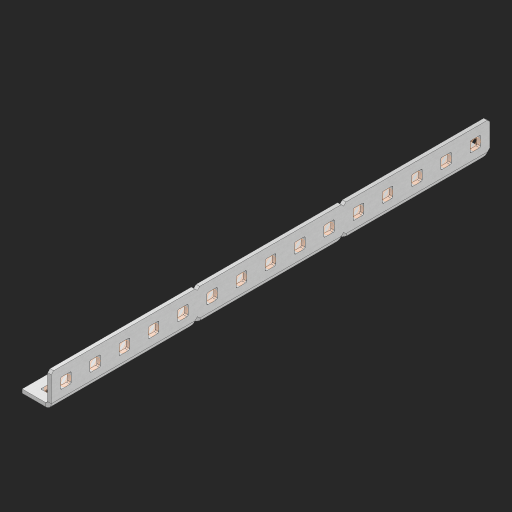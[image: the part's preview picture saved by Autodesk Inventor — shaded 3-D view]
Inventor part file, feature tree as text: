
AUTODESK INVENTOR PART (.ipt)
format: ipt  version: 2023 (Build 270158000, 158)  size: 598,528 bytes
history: native  units: in
note: dims shown in document units (in); Inventor stores cm internally (conversion verified against a paired STEP export)
features: other x35, extrude x29, sheet_metal_op x10, sketch x8, mirror x1, pattern_linear x1, chamfer x1
ambient origin geometry x8: Origin, YZ Plane, XZ Plane, XY Plane, X Axis, Y Axis, Z Axis, Center Point
bodies: Solid1 (feature_tree), Body (feature_tree)
feature tree (85):
  other  "Flange Pattern Plane"
  sheet_metal_op  "Flange Pattern"
  sheet_metal_op  "Body Pattern"
  other  "Arc Length"
  mirror  "Notch Mirror"
  pattern_linear  "Notch Pattern"  Spacing1=0.25in  [1 undecoded]
  chamfer  "End Chamfer"
  extrude  "Half Cut"  Depth=0.0625in
  sketch  "Sketch1"  dims[d0=1.5in]
  other  "Plate1"
  sketch  "Sketch2"  dims[d1=7.5in]
  other  "Plate2"
  sheet_metal_op  "Bend1"
  sheet_metal_op  "Corner1"
  sketch  "Sketch3"  dims[d2=0.0625in]
  other  "Flange Pattern Sketch"
  sketch  "Sketch7"  dims[d3=0.0625in]
  other  "Srf1"
  other  "Srf2"
  sketch  "Sketch8"  dims[d4=0.0312in]
  sketch  "Sketch9"  dims[d5=0.125in]
  other  "Srf91"
  sheet_metal_op  "Body Pattern Sketch"
  other  "Srf92"
  sketch  "Sketch13"  dims[d6=0.0625in]
  sketch  "Sketch14"  dims[d7=0.5in d8=90.0deg d9=0.0312in d10=0.25in d11=0.0625in d12=0.0625in d16=0.182in d17=0.02in d18=0.0625in d19=0.0in d20=0.25in d21=0.25in d46=0.172in d47=1.0in d48=0.0in d49=0.182in d50=0.02in d51=0.25in d52=0.25in d53=0.0625in d54=0.0in d55=0.172in d56=1.0in d57=0.0in d60=5.9055in d62=0.5in d63=0.3937in d65=0.5in d85=0.1473in d86=0.1782in d88=0.04in d89=0.0625in d90=0.0in d91=0.04in d92=0.0491in d95=2.5in d96=0.04in d97=0.25in d98=45.0deg d101=0.0in d102=2.497in d131=0.5in d132=5.9055in d134=0.5in d139=0.5in]
  other  "Srf856"
  other  "Srf1310"
  other  "Srf1311"
  other  "Srf1312"
  other  "Srf1376"
  other  "Srf1377"
  other  "Srf1728"
  other  "Srf1755"
  other  "Srf1878"
  other  "Srf1879"
  other  "Srf1880"
  other  "Srf1881"
  other  "Srf1882"
  other  "Srf1883"
  other  "Srf1884"
  other  "Srf1885"
  other  "Srf1886"
  other  "Srf1942"
  other  "Srf1943"
  other  "Srf1944"
  other  "Srf1945"
  other  "Srf1946"
  other  "Srf1947"
  other  "Srf1948"
  other  "Srf1949"
  other  "Srf1950"
  sheet_metal_op  "Flange Stamp"
  sheet_metal_op  "Flange Circle"
  sheet_metal_op  "Body Stamp"
  sheet_metal_op  "Body Circle"
  sheet_metal_op  "Notch"
  extrude  "ExtrusionSrf2"  Depth=0.0625in
  extrude  "ExtrusionSrf92"  Depth=0.5in
  extrude  "ExtrusionSrf856"  Depth=0.02in
  extrude  "ExtrusionSrf1310"  Depth=0.0625in
  extrude  "ExtrusionSrf1311"  TaperAngle=0.0deg  [1 undecoded]
  extrude  "ExtrusionSrf1312"  Depth=0.5in
  extrude  "ExtrusionSrf1376"  Depth=0.5in
  extrude  "ExtrusionSrf1377"  Depth=0.5in
  extrude  "ExtrusionSrf1728"  Depth=0.5in TaperAngle=0.0deg
  extrude  "ExtrusionSrf1755"  Depth=0.5in
  extrude  "ExtrusionSrf1878"  Depth=0.02in
  extrude  "ExtrusionSrf1879"  Depth=0.5in
  extrude  "ExtrusionSrf1880"  Depth=0.5in
  extrude  "ExtrusionSrf1881"  Depth=0.0625in
  extrude  "ExtrusionSrf1882"  TaperAngle=0.0deg  [1 undecoded]
  extrude  "ExtrusionSrf1883"  Depth=0.5in
  extrude  "ExtrusionSrf1884"  Depth=0.5in TaperAngle=0.0deg
  extrude  "ExtrusionSrf1885"  Depth=0.5in
  extrude  "ExtrusionSrf1886"  Depth=0.5in
  extrude  "ExtrusionSrf1942"  Depth=0.5in
  extrude  "ExtrusionSrf1943"  Depth=0.5in
  extrude  "ExtrusionSrf1944"  Depth=0.5in
  extrude  "ExtrusionSrf1945"  Depth=0.0625in
  extrude  "ExtrusionSrf1946"  TaperAngle=0.0deg  [1 undecoded]
  extrude  "ExtrusionSrf1947"  Depth=0.5in
  extrude  "ExtrusionSrf1948"  Depth=0.5in
  extrude  "ExtrusionSrf1949"  Depth=0.5in
  extrude  "ExtrusionSrf1950"  Depth=0.5in TaperAngle=45.0deg
note: 4 required parameter values undecoded (feature->parameter linkage not recoverable at this tier; creation-order binding heuristic only, values carry confidence <= 0.55)
